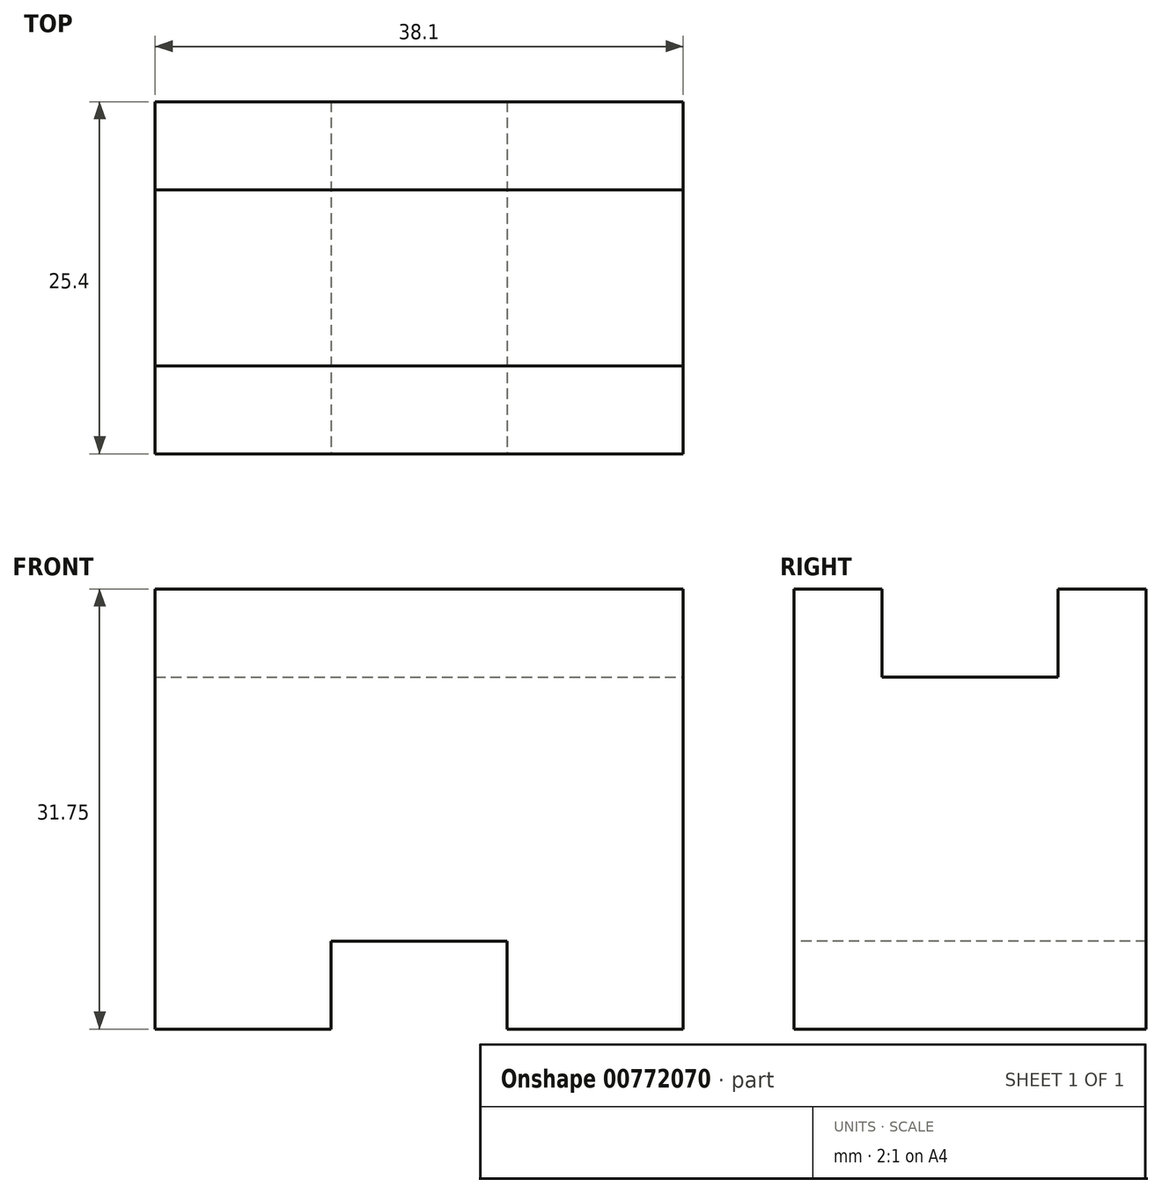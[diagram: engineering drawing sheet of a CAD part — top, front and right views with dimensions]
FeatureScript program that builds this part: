
annotation { "Feature Type Name" : "Feature", "Feature Type Description" : "" }
export const myFeature = defineFeature(function(context is Context, id is Id, definition is map)
    precondition{}
    {
        {
            var Q0;
            Q0=qCreatedBy(makeId("Front.planeOp"),FACE);
            var sketch = newSketch(context, id + "F0", { "sketchPlane" : qUnion([Q0])});
            skLineSegment(sketch, "E0", {"start": v(0, 0) * mm, "end": v(38.1, 0) * mm});
            skLineSegment(sketch, "E1", {"start": v(38.1, 0) * mm, "end": v(38.1, 31.75) * mm});
            skLineSegment(sketch, "E2", {"start": v(38.1, 31.75) * mm, "end": v(0, 31.75) * mm});
            skLineSegment(sketch, "E3", {"start": v(0, 31.75) * mm, "end": v(0, 0) * mm});
            skSolve(sketch);
        }
        {
            var Q0;
            Q0 = qSketchRegion(id + "F0", true);
            extrude(context, id + "F1", {"entities" : qUnion([Q0]), "depth" : 25.4 * mm, "offsetDistance" : 25.4 * mm});
        }
        {
            var Q0;
            Q0=makeQuery(id+"F1.opExtrude","CAP_FACE",FACE,{"disambiguationData":[OSD([sQuery(id+"F0.wireOp",EDGE,"E0"),sQuery(id+"F0.wireOp",EDGE,"E1"),sQuery(id+"F0.wireOp",EDGE,"E2"),sQuery(id+"F0.wireOp",EDGE,"E3")])],"isStart":false});
            var sketch = newSketch(context, id + "F2", { "sketchPlane" : qUnion([Q0])});
            skLineSegment(sketch, "E4", {"start": v(0, 0) * mm, "end": v(12.7, 0) * mm});
            skLineSegment(sketch, "E5", {"start": v(38.1, 0) * mm, "end": v(25.4, 0) * mm});
            skLineSegment(sketch, "E6", {"start": v(12.7, 0) * mm, "end": v(12.7, 6.35) * mm});
            skLineSegment(sketch, "E7", {"start": v(12.7, 6.35) * mm, "end": v(25.4, 6.35) * mm});
            skLineSegment(sketch, "E8", {"start": v(25.4, 0) * mm, "end": v(25.4, 6.35) * mm});
            skSolve(sketch);
        }
        {
            var Q0;
            {var subQ0=sQuery(id+"F2.wireOp",EDGE,"E6");Q0=makeQuery(id+"F2.imprint","IMPRINT",FACE,{"disambiguationData":[TD([[makeQuery(id+"F2.imprint","IMPRINT",EDGE,{"derivedFrom":subQ0}),-1.0]])]});}
            extrude(context, id + "F3", {"entities" : qUnion([Q0]), "operationType" : NewBodyOperationType.REMOVE, "oppositeDirection" : true, "depth" : 25.4 * mm, "offsetDistance" : 25.4 * mm});
        }
        {
            var Q0;
            Q0=makeQuery(id+"F1.opExtrude","SWEPT_FACE",FACE,{"disambiguationData":[OSD([sQuery(id+"F0.wireOp",EDGE,"E1")])]});
            var sketch = newSketch(context, id + "F4", { "sketchPlane" : qUnion([Q0])});
            skLineSegment(sketch, "E9", {"start": v(0, 31.75) * mm, "end": v(-6.35, 31.75) * mm});
            skLineSegment(sketch, "E10", {"start": v(-6.35, 31.75) * mm, "end": v(-6.35, 25.4) * mm});
            skLineSegment(sketch, "E11", {"start": v(-25.4, 31.75) * mm, "end": v(-19.05, 31.75) * mm});
            skLineSegment(sketch, "E12", {"start": v(-19.05, 31.75) * mm, "end": v(-19.05, 25.4) * mm});
            skLineSegment(sketch, "E13", {"start": v(-19.05, 25.4) * mm, "end": v(-6.35, 25.4) * mm});
            skSolve(sketch);
        }
        {
            var Q0;
            {var subQ0=sQuery(id+"F4.wireOp",EDGE,"E10");Q0=makeQuery(id+"F4.imprint","IMPRINT",FACE,{"disambiguationData":[TD([[makeQuery(id+"F4.imprint","IMPRINT",EDGE,{"derivedFrom":subQ0}),-1.0]])]});}
            extrude(context, id + "F5", {"entities" : qUnion([Q0]), "operationType" : NewBodyOperationType.REMOVE, "oppositeDirection" : true, "depth" : 25.4 * mm, "offsetDistance" : 25.4 * mm});
        }
        {
            var Q0;
            Q0=makeQuery(id+"F1.opExtrude","SWEPT_FACE",FACE,{"disambiguationData":[OSD([sQuery(id+"F0.wireOp",EDGE,"E3")])]});
            var sketch = newSketch(context, id + "F6", { "sketchPlane" : qUnion([Q0])});
            skLineSegment(sketch, "E14", {"start": v(25.4, 31.75) * mm, "end": v(19.05, 31.75) * mm});
            skLineSegment(sketch, "E15", {"start": v(0, 31.75) * mm, "end": v(6.35, 31.75) * mm});
            skLineSegment(sketch, "E16", {"start": v(6.35, 31.75) * mm, "end": v(6.35, 25.4) * mm});
            skLineSegment(sketch, "E17", {"start": v(19.05, 31.75) * mm, "end": v(19.05, 25.4) * mm});
            skLineSegment(sketch, "E18", {"start": v(19.05, 25.4) * mm, "end": v(6.35, 25.4) * mm});
            skSolve(sketch);
        }
        {
            var Q0;
            {var subQ0=sQuery(id+"F6.wireOp",EDGE,"E16");Q0=makeQuery(id+"F6.imprint","IMPRINT",FACE,{"disambiguationData":[TD([[makeQuery(id+"F6.imprint","IMPRINT",EDGE,{"derivedFrom":subQ0}),1.0]])]});}
            extrude(context, id + "F7", {"entities" : qUnion([Q0]), "operationType" : NewBodyOperationType.REMOVE, "oppositeDirection" : true, "depth" : 25.4 * mm, "offsetDistance" : 25.4 * mm});
        }
    });
